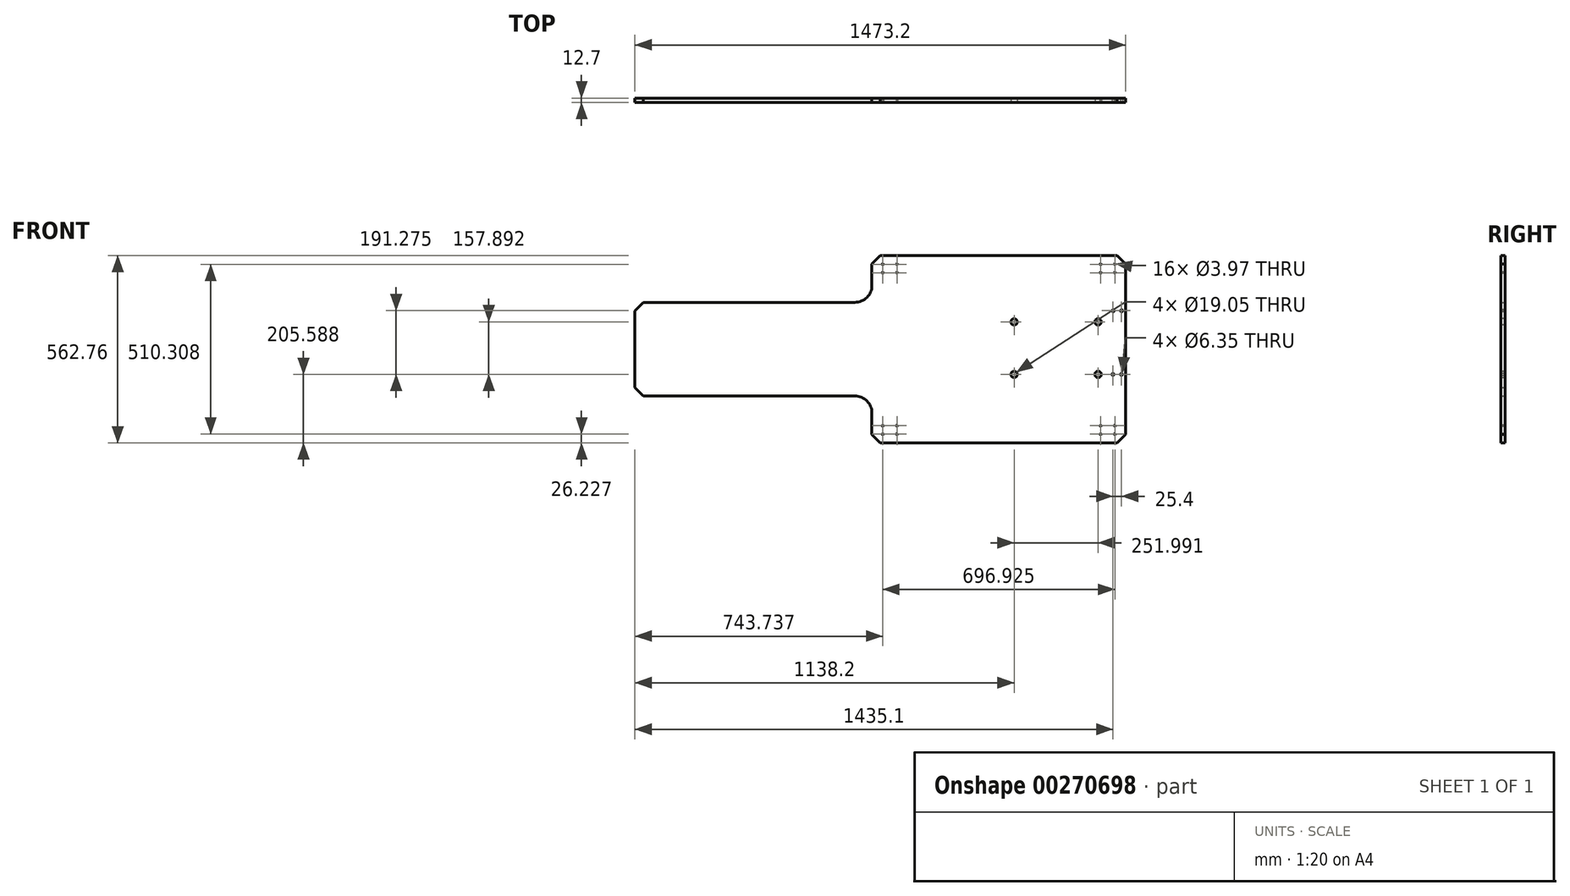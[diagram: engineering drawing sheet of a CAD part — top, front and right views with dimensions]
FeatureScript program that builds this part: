
annotation { "Feature Type Name" : "Feature", "Feature Type Description" : "" }
export const myFeature = defineFeature(function(context is Context, id is Id, definition is map)
    precondition{}
    {
        {
            var Q0;
            Q0=qCreatedBy(makeId("Front.planeOp"),FACE);
            var sketch = newSketch(context, id + "F0", { "sketchPlane" : qUnion([Q0])});
            skLineSegment(sketch, "E0.bottom", {"start": v(736.6, 0) * mm, "end": v(1447.8, 0) * mm});
            skLineSegment(sketch, "E0.top", {"start": v(736.6, 562.76) * mm, "end": v(1447.8, 562.76) * mm});
            skLineSegment(sketch, "E0.left", {"start": v(0, 166.1) * mm, "end": v(0, 396.67) * mm});
            skLineSegment(sketch, "E0.right", {"start": v(1473.2, 25.4) * mm, "end": v(1473.2, 537.36) * mm});
            skLineSegment(sketch, "E1", {"start": v(25.4, 140.7) * mm, "end": v(660.4, 140.7) * mm});
            skLineSegment(sketch, "E2", {"start": v(25.4, 422.07) * mm, "end": v(660.4, 422.07) * mm});
            skLineSegment(sketch, "E3", {"start": v(711.2, 472.87) * mm, "end": v(711.2, 537.36) * mm});
            skLineSegment(sketch, "E4", {"start": v(711.2, 89.9) * mm, "end": v(711.2, 25.4) * mm});
            skPoint(sketch, "E5.visualSharp", {"position": v(711.2, 422.07) * mm});
            skArc(sketch, "E5.filletArc", {"start": v(660.4, 422.07) * mm, "mid": v(696.32, 436.95) * mm, "end": v(711.2, 472.87) * mm});
            skPoint(sketch, "E6.visualSharp", {"position": v(711.2, 140.7) * mm});
            skArc(sketch, "E6.filletArc", {"start": v(711.2, 89.9) * mm, "mid": v(696.32, 125.81) * mm, "end": v(660.4, 140.7) * mm});
            skLineSegment(sketch, "E7", {"start": v(711.2, 537.36) * mm, "end": v(736.6, 562.76) * mm});
            skLineSegment(sketch, "E8", {"start": v(1447.8, 562.76) * mm, "end": v(1473.2, 537.36) * mm});
            skLineSegment(sketch, "E9", {"start": v(1447.8, 0) * mm, "end": v(1473.2, 25.4) * mm});
            skLineSegment(sketch, "E10", {"start": v(0, 396.67) * mm, "end": v(25.4, 422.07) * mm});
            skLineSegment(sketch, "E11", {"start": v(0, 166.1) * mm, "end": v(25.4, 140.7) * mm});
            skLineSegment(sketch, "E12", {"start": v(711.2, 25.4) * mm, "end": v(736.6, 0) * mm});
            skSolve(sketch);
        }
        {
            var Q0;
            Q0 = qSketchRegion(id + "F0", true);
            extrude(context, id + "F1", {"entities" : qUnion([Q0]), "depth" : 12.7 * mm});
        }
        {
            var Q0;
            Q0=makeQuery(id+"F1.opExtrude","CAP_FACE",FACE,{"disambiguationData":[OSD([sQuery(id+"F0.wireOp",EDGE,"E0.bottom"),sQuery(id+"F0.wireOp",EDGE,"E0.top"),sQuery(id+"F0.wireOp",EDGE,"E0.left"),sQuery(id+"F0.wireOp",EDGE,"E0.right"),sQuery(id+"F0.wireOp",EDGE,"E1"),sQuery(id+"F0.wireOp",EDGE,"E2"),sQuery(id+"F0.wireOp",EDGE,"E3"),sQuery(id+"F0.wireOp",EDGE,"E4"),sQuery(id+"F0.wireOp",EDGE,"E5.filletArc"),sQuery(id+"F0.wireOp",EDGE,"E6.filletArc"),sQuery(id+"F0.wireOp",EDGE,"E7"),sQuery(id+"F0.wireOp",EDGE,"E8"),sQuery(id+"F0.wireOp",EDGE,"E9"),sQuery(id+"F0.wireOp",EDGE,"E10"),sQuery(id+"F0.wireOp",EDGE,"E11"),sQuery(id+"F0.wireOp",EDGE,"E12")])],"isStart":false});
            var sketch = newSketch(context, id + "F2", { "sketchPlane" : qUnion([Q0])});
            skLineSegment(sketch, "E13", {"start": v(1473.2, 0) * mm, "end": v(1473.2, 205.59) * mm});
            skLineSegment(sketch, "E14", {"start": v(1473.2, 0) * mm, "end": v(1473.2, 383.39) * mm});
            skPoint(sketch, "E15", {"position": v(1435.1, 383.39) * mm});
            skPoint(sketch, "E16", {"position": v(1460.5, 383.39) * mm});
            skPoint(sketch, "E17", {"position": v(1435.1, 205.59) * mm});
            skPoint(sketch, "E18", {"position": v(1460.5, 205.59) * mm});
            skPoint(sketch, "E19", {"position": v(1390.2, 363.48) * mm});
            skPoint(sketch, "E20", {"position": v(1390.2, 205.59) * mm});
            skLineSegment(sketch, "E21", {"start": v(1138.2, 363.48) * mm, "end": v(1138.2, 205.59) * mm});
            skPoint(sketch, "E22", {"position": v(1138.2, 363.48) * mm});
            skPoint(sketch, "E23", {"position": v(1138.2, 205.59) * mm});
            skLineSegment(sketch, "E24", {"start": v(1390.2, 205.59) * mm, "end": v(1390.2, 363.48) * mm});
            skLineSegment(sketch, "E25", {"start": v(1435.1, 383.39) * mm, "end": v(1460.5, 383.39) * mm});
            skLineSegment(sketch, "E26", {"start": v(1460.5, 383.39) * mm, "end": v(1473.2, 383.39) * mm});
            skSolve(sketch);
        }
        {
            var Q0;
            Q0=sQuery(id+"F2.wireOp",VERTEX,"E22");
            var Q1;
            Q1=sQuery(id+"F2.wireOp",VERTEX,"E23");
            var Q2;
            Q2=sQuery(id+"F2.wireOp",VERTEX,"E20");
            var Q3;
            Q3=sQuery(id+"F2.wireOp",VERTEX,"E19");
            var Q4;
            Q4=makeQuery(id+"F1.opExtrude","SWEPT_BODY",BODY,{"disambiguationData":[OSD([sQuery(id+"F0.wireOp",EDGE,"E0.bottom"),sQuery(id+"F0.wireOp",EDGE,"E0.top"),sQuery(id+"F0.wireOp",EDGE,"E0.left"),sQuery(id+"F0.wireOp",EDGE,"E0.right"),sQuery(id+"F0.wireOp",EDGE,"E1"),sQuery(id+"F0.wireOp",EDGE,"E2"),sQuery(id+"F0.wireOp",EDGE,"E3"),sQuery(id+"F0.wireOp",EDGE,"E4"),sQuery(id+"F0.wireOp",EDGE,"E5.filletArc"),sQuery(id+"F0.wireOp",EDGE,"E6.filletArc"),sQuery(id+"F0.wireOp",EDGE,"E7"),sQuery(id+"F0.wireOp",EDGE,"E8"),sQuery(id+"F0.wireOp",EDGE,"E9"),sQuery(id+"F0.wireOp",EDGE,"E10"),sQuery(id+"F0.wireOp",EDGE,"E11"),sQuery(id+"F0.wireOp",EDGE,"E12")])]});
            hole(context, id + "F3", {"style" : HoleStyle.SIMPLE, "endStyle" : HoleEndStyle.THROUGH, "holeDiameter" : 19.05 * mm, "tappedDepth" : 12.7 * mm, "tapClearance" : 3, "locations" : qUnion([Q0, Q1, Q2, Q3]), "scope" : qUnion([Q4])});
        }
        {
            var Q0;
            Q0=makeQuery(id+"F1.opExtrude","CAP_FACE",FACE,{"disambiguationData":[OSD([sQuery(id+"F0.wireOp",EDGE,"E0.bottom"),sQuery(id+"F0.wireOp",EDGE,"E0.top"),sQuery(id+"F0.wireOp",EDGE,"E0.left"),sQuery(id+"F0.wireOp",EDGE,"E0.right"),sQuery(id+"F0.wireOp",EDGE,"E1"),sQuery(id+"F0.wireOp",EDGE,"E2"),sQuery(id+"F0.wireOp",EDGE,"E3"),sQuery(id+"F0.wireOp",EDGE,"E4"),sQuery(id+"F0.wireOp",EDGE,"E5.filletArc"),sQuery(id+"F0.wireOp",EDGE,"E6.filletArc"),sQuery(id+"F0.wireOp",EDGE,"E7"),sQuery(id+"F0.wireOp",EDGE,"E8"),sQuery(id+"F0.wireOp",EDGE,"E9"),sQuery(id+"F0.wireOp",EDGE,"E10"),sQuery(id+"F0.wireOp",EDGE,"E11"),sQuery(id+"F0.wireOp",EDGE,"E12")])],"isStart":false});
            var sketch = newSketch(context, id + "F4", { "sketchPlane" : qUnion([Q0])});
            skPoint(sketch, "E27", {"position": v(1435.1, 396.86) * mm});
            skPoint(sketch, "E28", {"position": v(1460.5, 396.86) * mm});
            skPoint(sketch, "E29.MirrorP", {"position": v(1435.1, 205.59) * mm});
            skPoint(sketch, "E30.MirrorP", {"position": v(1460.5, 205.59) * mm});
            skLineSegment(sketch, "E31", {"start": v(1435.1, 396.86) * mm, "end": v(1460.5, 396.86) * mm});
            skSolve(sketch);
        }
        {
            var Q0;
            Q0=sQuery(id+"F4.wireOp",VERTEX,"E27");
            var Q1;
            Q1=sQuery(id+"F4.wireOp",VERTEX,"E28");
            var Q2;
            Q2=sQuery(id+"F4.wireOp",VERTEX,"E29.MirrorP");
            var Q3;
            Q3=sQuery(id+"F4.wireOp",VERTEX,"E30.MirrorP");
            var Q4;
            Q4=makeQuery(id+"F1.opExtrude","SWEPT_BODY",BODY,{"disambiguationData":[OSD([sQuery(id+"F0.wireOp",EDGE,"E0.bottom"),sQuery(id+"F0.wireOp",EDGE,"E0.top"),sQuery(id+"F0.wireOp",EDGE,"E0.left"),sQuery(id+"F0.wireOp",EDGE,"E0.right"),sQuery(id+"F0.wireOp",EDGE,"E1"),sQuery(id+"F0.wireOp",EDGE,"E2"),sQuery(id+"F0.wireOp",EDGE,"E3"),sQuery(id+"F0.wireOp",EDGE,"E4"),sQuery(id+"F0.wireOp",EDGE,"E5.filletArc"),sQuery(id+"F0.wireOp",EDGE,"E6.filletArc"),sQuery(id+"F0.wireOp",EDGE,"E7"),sQuery(id+"F0.wireOp",EDGE,"E8"),sQuery(id+"F0.wireOp",EDGE,"E9"),sQuery(id+"F0.wireOp",EDGE,"E10"),sQuery(id+"F0.wireOp",EDGE,"E11"),sQuery(id+"F0.wireOp",EDGE,"E12")])]});
            hole(context, id + "F5", {"style" : HoleStyle.SIMPLE, "endStyle" : HoleEndStyle.THROUGH, "holeDiameter" : 6.35 * mm, "tappedDepth" : 12.7 * mm, "tapClearance" : 3, "locations" : qUnion([Q0, Q1, Q2, Q3]), "scope" : qUnion([Q4])});
        }
        {
            var Q0;
            Q0=makeQuery(id+"F1.opExtrude","CAP_FACE",FACE,{"disambiguationData":[OSD([sQuery(id+"F0.wireOp",EDGE,"E0.bottom"),sQuery(id+"F0.wireOp",EDGE,"E0.top"),sQuery(id+"F0.wireOp",EDGE,"E0.left"),sQuery(id+"F0.wireOp",EDGE,"E0.right"),sQuery(id+"F0.wireOp",EDGE,"E1"),sQuery(id+"F0.wireOp",EDGE,"E2"),sQuery(id+"F0.wireOp",EDGE,"E3"),sQuery(id+"F0.wireOp",EDGE,"E4"),sQuery(id+"F0.wireOp",EDGE,"E5.filletArc"),sQuery(id+"F0.wireOp",EDGE,"E6.filletArc"),sQuery(id+"F0.wireOp",EDGE,"E7"),sQuery(id+"F0.wireOp",EDGE,"E8"),sQuery(id+"F0.wireOp",EDGE,"E9"),sQuery(id+"F0.wireOp",EDGE,"E10"),sQuery(id+"F0.wireOp",EDGE,"E11"),sQuery(id+"F0.wireOp",EDGE,"E12")])],"isStart":false});
            var sketch = newSketch(context, id + "F6", { "sketchPlane" : qUnion([Q0])});
            skPoint(sketch, "E32", {"position": v(739.77, 545.26) * mm});
            skPoint(sketch, "E33", {"position": v(790.57, 502.41) * mm});
            skPoint(sketch, "E34", {"position": v(743.74, 536.54) * mm});
            skPoint(sketch, "E35", {"position": v(743.74, 511.14) * mm});
            skPoint(sketch, "E36.MirrorP", {"position": v(786.61, 536.54) * mm});
            skPoint(sketch, "E37.MirrorP", {"position": v(786.61, 511.14) * mm});
            skPoint(sketch, "E38.endSnap0", {"position": v(1473.2, 281.38) * mm});
            skPoint(sketch, "E39.MirrorP", {"position": v(743.74, 51.63) * mm});
            skPoint(sketch, "E40.MirrorP", {"position": v(743.74, 26.23) * mm});
            skPoint(sketch, "E41.MirrorP", {"position": v(786.61, 26.23) * mm});
            skPoint(sketch, "E42.MirrorP", {"position": v(786.61, 51.63) * mm});
            skPoint(sketch, "E43.MirrorP", {"position": v(1397.79, 26.23) * mm});
            skPoint(sketch, "E44.MirrorP", {"position": v(1440.66, 51.63) * mm});
            skPoint(sketch, "E45.MirrorP", {"position": v(1440.66, 26.23) * mm});
            skPoint(sketch, "E46.MirrorP", {"position": v(1397.79, 51.63) * mm});
            skPoint(sketch, "E47.MirrorP", {"position": v(1440.66, 511.14) * mm});
            skPoint(sketch, "E48.MirrorP", {"position": v(1440.66, 536.54) * mm});
            skPoint(sketch, "E49.MirrorP", {"position": v(1397.79, 536.54) * mm});
            skPoint(sketch, "E50.MirrorP", {"position": v(1397.79, 511.14) * mm});
            skSolve(sketch);
        }
        {
            var Q0;
            Q0=sQuery(id+"F6.wireOp",VERTEX,"E34");
            var Q1;
            Q1=sQuery(id+"F6.wireOp",VERTEX,"E35");
            var Q2;
            Q2=sQuery(id+"F6.wireOp",VERTEX,"E37.MirrorP");
            var Q3;
            Q3=sQuery(id+"F6.wireOp",VERTEX,"E36.MirrorP");
            var Q4;
            Q4=sQuery(id+"F6.wireOp",VERTEX,"E40.MirrorP");
            var Q5;
            Q5=sQuery(id+"F6.wireOp",VERTEX,"E39.MirrorP");
            var Q6;
            Q6=sQuery(id+"F6.wireOp",VERTEX,"E42.MirrorP");
            var Q7;
            Q7=sQuery(id+"F6.wireOp",VERTEX,"E41.MirrorP");
            var Q8;
            Q8=sQuery(id+"F6.wireOp",VERTEX,"E43.MirrorP");
            var Q9;
            Q9=sQuery(id+"F6.wireOp",VERTEX,"E46.MirrorP");
            var Q10;
            Q10=sQuery(id+"F6.wireOp",VERTEX,"E45.MirrorP");
            var Q11;
            Q11=sQuery(id+"F6.wireOp",VERTEX,"E44.MirrorP");
            var Q12;
            Q12=sQuery(id+"F6.wireOp",VERTEX,"E50.MirrorP");
            var Q13;
            Q13=sQuery(id+"F6.wireOp",VERTEX,"E49.MirrorP");
            var Q14;
            Q14=sQuery(id+"F6.wireOp",VERTEX,"E48.MirrorP");
            var Q15;
            Q15=sQuery(id+"F6.wireOp",VERTEX,"E47.MirrorP");
            var Q16;
            Q16=makeQuery(id+"F1.opExtrude","SWEPT_BODY",BODY,{"disambiguationData":[OSD([sQuery(id+"F0.wireOp",EDGE,"E0.bottom"),sQuery(id+"F0.wireOp",EDGE,"E0.top"),sQuery(id+"F0.wireOp",EDGE,"E0.left"),sQuery(id+"F0.wireOp",EDGE,"E0.right"),sQuery(id+"F0.wireOp",EDGE,"E1"),sQuery(id+"F0.wireOp",EDGE,"E2"),sQuery(id+"F0.wireOp",EDGE,"E3"),sQuery(id+"F0.wireOp",EDGE,"E4"),sQuery(id+"F0.wireOp",EDGE,"E5.filletArc"),sQuery(id+"F0.wireOp",EDGE,"E6.filletArc"),sQuery(id+"F0.wireOp",EDGE,"E7"),sQuery(id+"F0.wireOp",EDGE,"E8"),sQuery(id+"F0.wireOp",EDGE,"E9"),sQuery(id+"F0.wireOp",EDGE,"E10"),sQuery(id+"F0.wireOp",EDGE,"E11"),sQuery(id+"F0.wireOp",EDGE,"E12")])]});
            hole(context, id + "F7", {"style" : HoleStyle.SIMPLE, "endStyle" : HoleEndStyle.THROUGH, "holeDiameter" : 3.97 * mm, "tappedDepth" : 12.7 * mm, "tapClearance" : 3, "locations" : qUnion([Q0, Q1, Q2, Q3, Q4, Q5, Q6, Q7, Q8, Q9, Q10, Q11, Q12, Q13, Q14, Q15]), "scope" : qUnion([Q16])});
        }
    });
